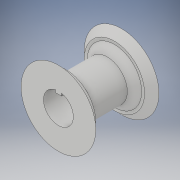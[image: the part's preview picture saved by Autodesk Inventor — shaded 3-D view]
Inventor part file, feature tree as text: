
AUTODESK INVENTOR PART (.ipt)
format: ipt  version: 2017 (Build 210142000, 142)  size: 159,744 bytes
history: native  units: in
note: dims shown in document units (in); Inventor stores cm internally (conversion verified against a paired STEP export)
features: extrude x7, sketch x7, chamfer x1
ambient origin geometry x8: Origin, YZ Plane, XZ Plane, XY Plane, X Axis, Y Axis, Z Axis, Center Point
bodies: Solid1 (feature_tree)
feature tree (15):
  extrude  "Extrusion1"  Depth=1.3in
  extrude  "Extrusion2"  Depth=1.0in
  extrude  "Extrusion3"  Depth=1.0in
  extrude  "Extrusion4"  Depth=0.52in
  extrude  "Extrusion5"  Depth=0.108in
  extrude  "Extrusion6"  Depth=1.1in TaperAngle=0.0deg
  extrude  "Extrusion7"  Depth=0.125in TaperAngle=0.0deg
  chamfer  "Chamfer1"  Distance=1.0in
  sketch  "Sketch1"  dims[d0=0.52in d1=1.3in]
  sketch  "Sketch2"  dims[d2=0.25in d3=0.0in d4=1.0in]
  sketch  "Sketch3"  dims[d5=0.6in d6=0.0in d7=1.0in]
  sketch  "Sketch4"  dims[d8=1.3in d9=0.52in]
  sketch  "Sketch5"  dims[d10=0.25in d11=0.0in d12=0.108in]
  sketch  "Sketch6"  dims[d13=0.05in d14=1.1in d15=0.0in]
  sketch  "Sketch7"  dims[d16=1.3in d17=0.125in d18=0.0in d19=1.0in d20=1.3in d21=0.125in d22=0.0in d23=0.7in d24=1.0in d25=0.85in d26=0.0in d27=0.125in d28=0.125in d29=45.0deg]
